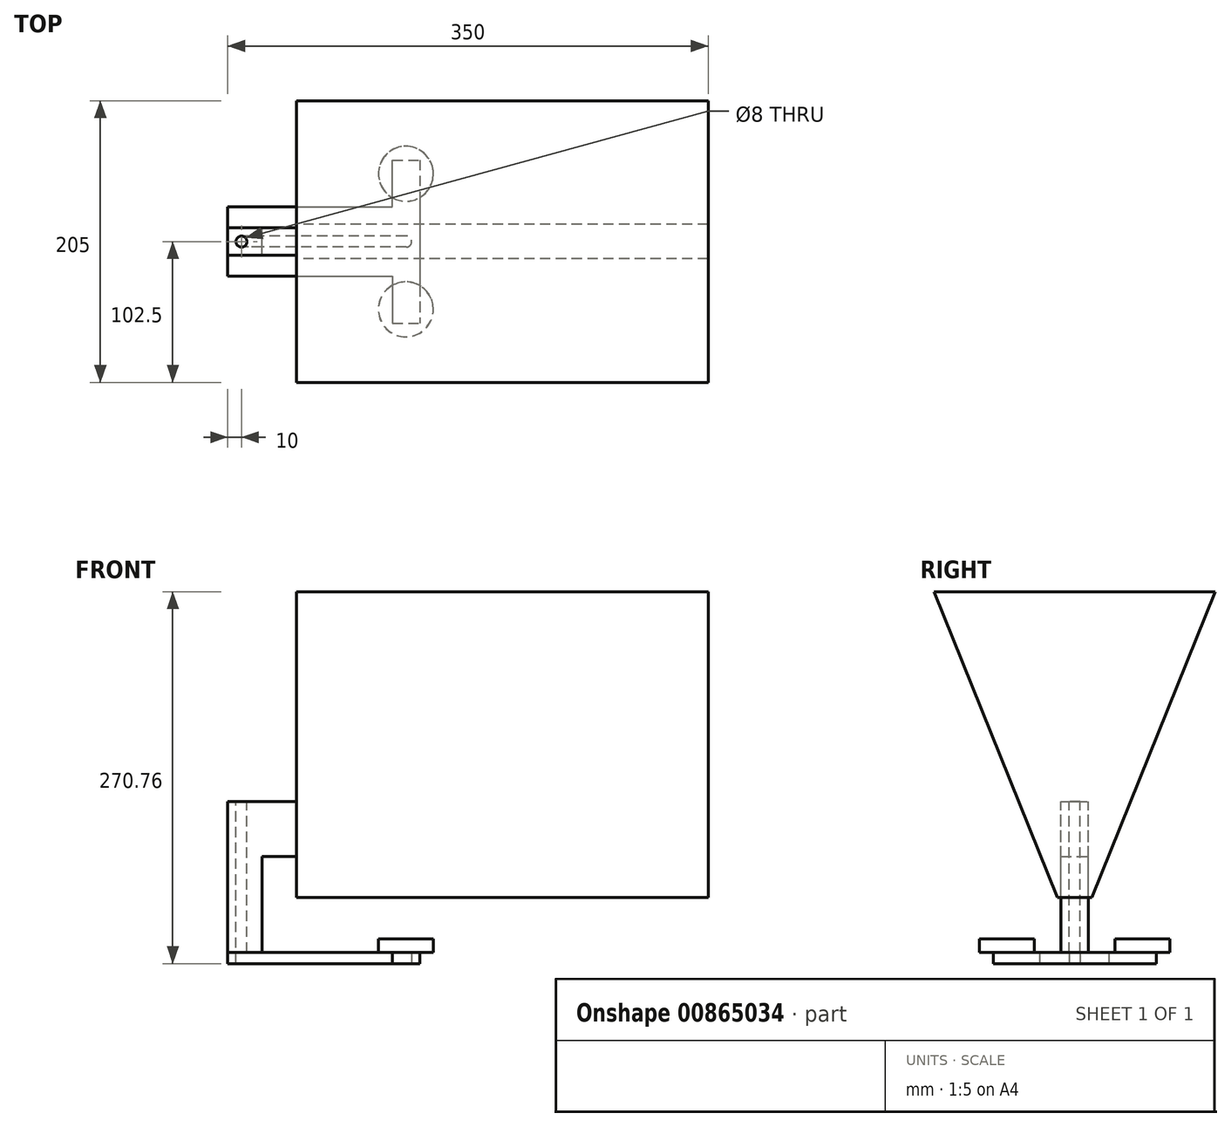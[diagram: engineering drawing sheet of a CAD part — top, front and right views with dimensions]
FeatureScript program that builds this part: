
annotation { "Feature Type Name" : "Feature", "Feature Type Description" : "" }
export const myFeature = defineFeature(function(context is Context, id is Id, definition is map)
    precondition{}
    {
        {
            var Q0;
            Q0=qCreatedBy(makeId("Right.planeOp"),FACE);
            var sketch = newSketch(context, id + "F0", { "sketchPlane" : qUnion([Q0])});
            skLineSegment(sketch, "E0", {"start": v(-102.5, 222.76) * mm, "end": v(-12.5, 0) * mm});
            skLineSegment(sketch, "E1", {"start": v(-12.5, 0) * mm, "end": v(0, 0) * mm});
            skLineSegment(sketch, "E2", {"start": v(-102.5, 222.76) * mm, "end": v(0, 222.76) * mm});
            skLineSegment(sketch, "E3.MirrorCS", {"start": v(12.5, 0) * mm, "end": v(0, 0) * mm});
            skLineSegment(sketch, "E4.MirrorCS", {"start": v(102.5, 222.76) * mm, "end": v(12.5, 0) * mm});
            skLineSegment(sketch, "E5.MirrorCS", {"start": v(102.5, 222.76) * mm, "end": v(0, 222.76) * mm});
            skSolve(sketch);
        }
        {
            var Q0;
            Q0 = qSketchRegion(id + "F0", true);
            extrude(context, id + "F1", {"entities" : qUnion([Q0]), "depth" : 300 * mm, "offsetDistance" : 25 * mm});
        }
        {
            var Q0;
            Q0=makeQuery(id+"F1.opExtrude","CAP_FACE",FACE,{"disambiguationData":[OSD([sQuery(id+"F0.wireOp",EDGE,"E0"),sQuery(id+"F0.wireOp",EDGE,"E1"),sQuery(id+"F0.wireOp",EDGE,"E2"),sQuery(id+"F0.wireOp",EDGE,"E3.MirrorCS"),sQuery(id+"F0.wireOp",EDGE,"E4.MirrorCS"),sQuery(id+"F0.wireOp",EDGE,"E5.MirrorCS")])],"isStart":true});
            var sketch = newSketch(context, id + "F2", { "sketchPlane" : qUnion([Q0])});
            skLineSegment(sketch, "E6.bottom", {"start": v(10, 30) * mm, "end": v(-10, 30) * mm});
            skLineSegment(sketch, "E6.top", {"start": v(10, 70) * mm, "end": v(-10, 70) * mm});
            skLineSegment(sketch, "E6.left", {"start": v(10, 30) * mm, "end": v(10, 70) * mm});
            skLineSegment(sketch, "E6.right", {"start": v(-10, 30) * mm, "end": v(-10, 70) * mm});
            skPoint(sketch, "E6.middle", {"position": v(0, 50) * mm});
            skSolve(sketch);
        }
        {
            var Q0;
            Q0 = qSketchRegion(id + "F2", true);
            extrude(context, id + "F3", {"entities" : qUnion([Q0]), "operationType" : NewBodyOperationType.ADD, "depth" : 50 * mm, "offsetDistance" : 25 * mm});
        }
        {
            var Q0;
            Q0=makeQuery(id+"F3.opExtrude","SWEPT_FACE",FACE,{"disambiguationData":[OSD([sQuery(id+"F2.wireOp",EDGE,"E6.top")])]});
            var sketch = newSketch(context, id + "F4", { "sketchPlane" : qUnion([Q0])});
            skCircle(sketch, "E7", {"center": v(-40, 0) * mm, "radius": 4 * mm});
            skSolve(sketch);
        }
        {
            var Q0;
            Q0=makeQuery(id+"F3.opExtrude","SWEPT_FACE",FACE,{"disambiguationData":[OSD([sQuery(id+"F2.wireOp",EDGE,"E6.bottom")])]});
            var sketch = newSketch(context, id + "F5", { "sketchPlane" : qUnion([Q0])});
            skLineSegment(sketch, "E8", {"start": v(-50, 10) * mm, "end": v(-25, 10) * mm});
            skLineSegment(sketch, "E9", {"start": v(-25, 10) * mm, "end": v(-25, -10) * mm});
            skLineSegment(sketch, "E10", {"start": v(-25, -10) * mm, "end": v(-50, -10) * mm});
            skLineSegment(sketch, "E11", {"start": v(-50, -10) * mm, "end": v(-50, 10) * mm});
            skSolve(sketch);
        }
        {
            var Q0;
            Q0 = qSketchRegion(id + "F5", true);
            extrude(context, id + "F6", {"entities" : qUnion([Q0]), "operationType" : NewBodyOperationType.ADD, "depth" : 70 * mm, "offsetDistance" : 25 * mm});
        }
        {
            var Q0;
            Q0=makeQuery(id+"F4.imprint","IMPRINT",FACE,{"disambiguationData":[TD([[makeQuery(id+"F4.imprint","IMPRINT",EDGE,{"derivedFrom":sQuery(id+"F4.wireOp",EDGE,"E7")}),-1.0]])]});
            var sketch = newSketch(context, id + "F7", { "sketchPlane" : qUnion([Q0])});
            skSolve(sketch);
        }
        {
            var Q0;
            Q0=makeQuery(id+"F7.imprint","IMPRINT",FACE,{"disambiguationData":[TD([[makeQuery(id+"F7.imprint","IMPRINT",EDGE,{"derivedFrom":makeQuery(id+"F4.imprint","IMPRINT",EDGE,{"derivedFrom":sQuery(id+"F4.wireOp",EDGE,"E7")})}),1.0]])]});
            var Q1;
            Q1=sQuery(id+"F4.wireOp",EDGE,"E7");
            extrude(context, id + "F8", {"entities" : qUnion([Q0]), "operationType" : NewBodyOperationType.REMOVE, "surfaceEntities" : qUnion([Q1]), "oppositeDirection" : true, "depth" : 120 * mm, "offsetDistance" : 25 * mm});
        }
        {
            var Q0;
            Q0=makeQuery(id+"F6.opExtrude","CAP_FACE",FACE,{"disambiguationData":[OSD([sQuery(id+"F5.wireOp",EDGE,"E8"),sQuery(id+"F5.wireOp",EDGE,"E9"),sQuery(id+"F5.wireOp",EDGE,"E10"),sQuery(id+"F5.wireOp",EDGE,"E11")])],"isStart":false});
            var sketch = newSketch(context, id + "F9", { "sketchPlane" : qUnion([Q0])});
            skLineSegment(sketch, "E12", {"start": v(-50, -25.2) * mm, "end": v(70, -25.2) * mm});
            skLineSegment(sketch, "E13", {"start": v(70, -25.2) * mm, "end": v(70, -59.38) * mm});
            skLineSegment(sketch, "E14", {"start": v(70, -59.38) * mm, "end": v(90, -59.38) * mm});
            skLineSegment(sketch, "E15", {"start": v(90, -59.38) * mm, "end": v(90, 0) * mm});
            skLineSegment(sketch, "E16", {"start": v(-50, -25.2) * mm, "end": v(-50, 0) * mm});
            skLineSegment(sketch, "E17.MirrorCS", {"start": v(-50, 25.2) * mm, "end": v(-50, 0) * mm});
            skLineSegment(sketch, "E18.MirrorCS", {"start": v(-50, 25.2) * mm, "end": v(70, 25.2) * mm});
            skLineSegment(sketch, "E19.MirrorCS", {"start": v(70, 25.2) * mm, "end": v(70, 59.38) * mm});
            skLineSegment(sketch, "E20.MirrorCS", {"start": v(90, 59.38) * mm, "end": v(90, 0) * mm});
            skLineSegment(sketch, "E21.MirrorCS", {"start": v(70, 59.38) * mm, "end": v(90, 59.38) * mm});
            skSolve(sketch);
        }
        {
            var Q0;
            Q0 = qSketchRegion(id + "F9", true);
            extrude(context, id + "F10", {"entities" : qUnion([Q0]), "operationType" : NewBodyOperationType.ADD, "depth" : 8 * mm, "offsetDistance" : 25 * mm});
        }
        {
            var Q0;
            {var subQ0=sQuery(id+"F9.wireOp",EDGE,"E13");var subQ1=sQuery(id+"F9.wireOp",EDGE,"E14");var subQ2=sQuery(id+"F9.wireOp",EDGE,"E12");var subQ4=sQuery(id+"F2.wireOp",EDGE,"E6.left");var subQ5=sQuery(id+"F9.wireOp",EDGE,"E20.MirrorCS");var subQ6=sQuery(id+"F9.wireOp",EDGE,"E15");var subQ7=sQuery(id+"F9.wireOp",EDGE,"E18.MirrorCS");var subQ8=sQuery(id+"F9.wireOp",EDGE,"E19.MirrorCS");var subQ9=sQuery(id+"F9.wireOp",EDGE,"E17.MirrorCS");var subQ10=sQuery(id+"F9.wireOp",EDGE,"E16");var subQ11=sQuery(id+"F9.wireOp",EDGE,"E21.MirrorCS");Q0=makeQuery(id+"F10.boolean.opBoolean","SPLIT",FACE,{"disambiguationData":[TD([makeQuery(id+"F3.opExtrude","SWEPT_FACE",FACE,{"disambiguationData":[OSD([subQ4])]})])],"derivedFrom":makeQuery(id+"F10.opExtrude","CAP_FACE",FACE,{"disambiguationData":[OSD([subQ2,subQ0,subQ1,subQ6,subQ10,subQ9,subQ7,subQ8,subQ5,subQ11])],"isStart":true})});}
            var sketch = newSketch(context, id + "F11", { "sketchPlane" : qUnion([Q0])});
            skCircle(sketch, "E22", {"center": v(79.76, -49.38) * mm, "radius": 20 * mm});
            skCircle(sketch, "E23.MirrorC", {"center": v(79.76, 49.38) * mm, "radius": 20 * mm});
            skSolve(sketch);
        }
        {
            var Q0;
            Q0 = qSketchRegion(id + "F11", true);
            extrude(context, id + "F12", {"entities" : qUnion([Q0]), "operationType" : NewBodyOperationType.ADD, "depth" : 10 * mm, "offsetDistance" : 25 * mm});
        }
        {
            var Q0;
            Q0=makeQuery(id+"F10.opExtrude","CAP_FACE",FACE,{"disambiguationData":[OSD([sQuery(id+"F9.wireOp",EDGE,"E12"),sQuery(id+"F9.wireOp",EDGE,"E13"),sQuery(id+"F9.wireOp",EDGE,"E14"),sQuery(id+"F9.wireOp",EDGE,"E15"),sQuery(id+"F9.wireOp",EDGE,"E16"),sQuery(id+"F9.wireOp",EDGE,"E17.MirrorCS"),sQuery(id+"F9.wireOp",EDGE,"E18.MirrorCS"),sQuery(id+"F9.wireOp",EDGE,"E19.MirrorCS"),sQuery(id+"F9.wireOp",EDGE,"E20.MirrorCS"),sQuery(id+"F9.wireOp",EDGE,"E21.MirrorCS")])],"isStart":false});
            var sketch = newSketch(context, id + "F13", { "sketchPlane" : qUnion([Q0])});
            skLineSegment(sketch, "E24.bottom", {"start": v(80, 4) * mm, "end": v(-40, 4) * mm});
            skLineSegment(sketch, "E24.top", {"start": v(80, -4) * mm, "end": v(-40, -4) * mm});
            skPoint(sketch, "E24.middle", {"position": v(20, 0) * mm});
            skArc(sketch, "E25", {"start": v(-40, 4) * mm, "mid": v(-44, 0) * mm, "end": v(-40, -4) * mm});
            skArc(sketch, "E26", {"start": v(80, -4) * mm, "mid": v(84, 0) * mm, "end": v(80, 4) * mm});
            skSolve(sketch);
        }
        {
            var Q0;
            Q0 = qSketchRegion(id + "F13", true);
            extrude(context, id + "F14", {"entities" : qUnion([Q0]), "operationType" : NewBodyOperationType.REMOVE, "oppositeDirection" : true, "depth" : 8 * mm, "offsetDistance" : 25 * mm});
        }
    });
